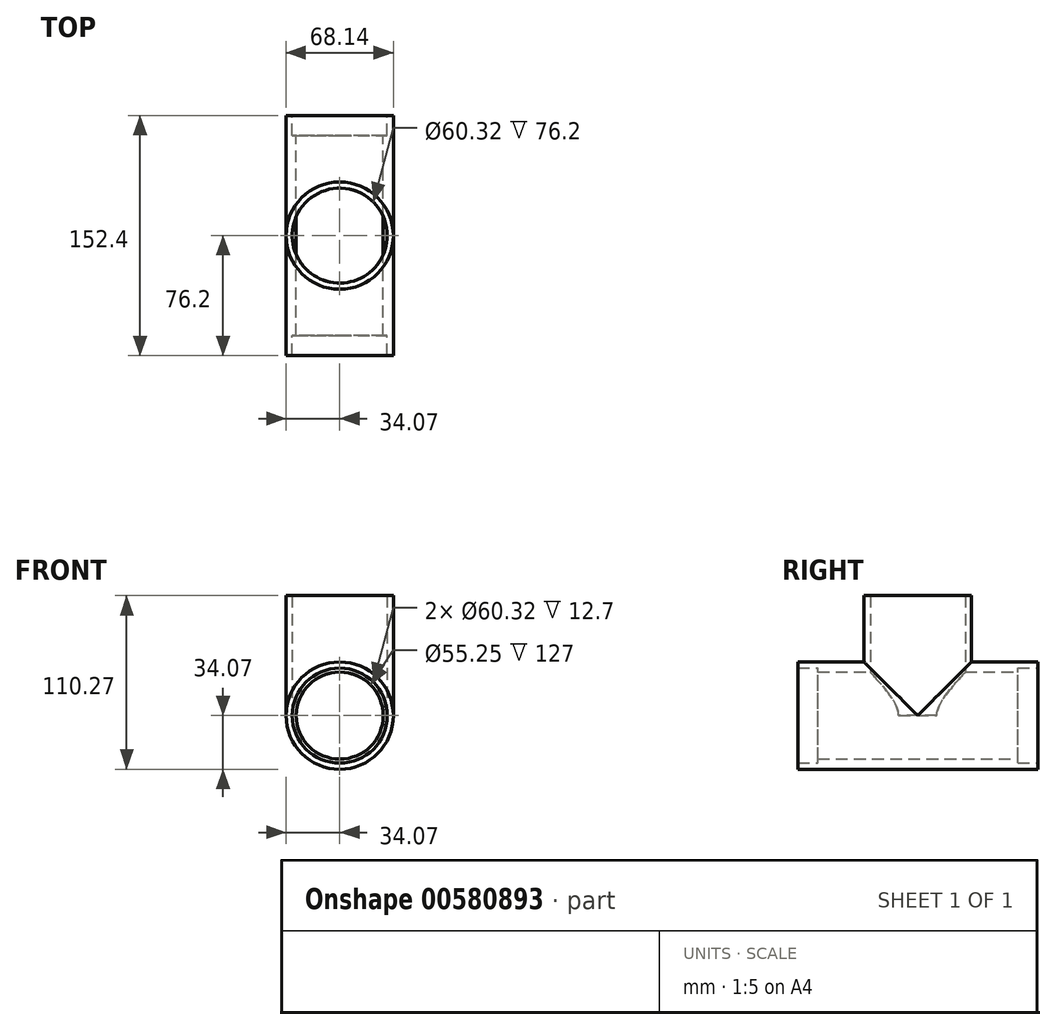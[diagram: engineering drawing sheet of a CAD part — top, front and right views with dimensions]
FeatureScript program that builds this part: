
annotation { "Feature Type Name" : "Feature", "Feature Type Description" : "" }
export const myFeature = defineFeature(function(context is Context, id is Id, definition is map)
    precondition{}
    {
        {
            var Q0;
            Q0=qCreatedBy(makeId("Front.planeOp"),FACE);
            var sketch = newSketch(context, id + "F0", { "sketchPlane" : qUnion([Q0])});
            skCircle(sketch, "E0", {"center": v(0, 0) * mm, "radius": 30.16 * mm});
            skCircle(sketch, "E1.0", {"center": v(0, 0) * mm, "radius": 34.07 * mm});
            skSolve(sketch);
        }
        {
            var Q0;
            Q0 = qSketchRegion(id + "F0", true);
            extrude(context, id + "F1", {"entities" : qUnion([Q0]), "endBound" : BoundingType.SYMMETRIC, "depth" : 152.4 * mm, "offsetDistance" : 25 * mm});
        }
        {
            var Q0;
            Q0=qCreatedBy(makeId("Top.planeOp"),FACE);
            var sketch = newSketch(context, id + "F2", { "sketchPlane" : qUnion([Q0])});
            skCircle(sketch, "E2", {"center": v(0, 0) * mm, "radius": 30.16 * mm});
            skCircle(sketch, "E3.0", {"center": v(0, 0) * mm, "radius": 34.07 * mm});
            skSolve(sketch);
        }
        {
            var Q0;
            Q0 = qSketchRegion(id + "F2", true);
            extrude(context, id + "F3", {"entities" : qUnion([Q0]), "operationType" : NewBodyOperationType.ADD, "depth" : 76.2 * mm, "offsetDistance" : 25 * mm});
        }
        {
            var Q0;
            Q0=qCreatedBy(makeId("Front.planeOp"),FACE);
            var sketch = newSketch(context, id + "F4", { "sketchPlane" : qUnion([Q0])});
            skCircle(sketch, "E4.0", {"center": v(0, 0) * mm, "radius": 27.62 * mm});
            skCircle(sketch, "E5.0", {"center": v(0, 0) * mm, "radius": 34.07 * mm});
            skSolve(sketch);
        }
        {
            var Q0;
            Q0 = qSketchRegion(id + "F4", true);
            extrude(context, id + "F5", {"entities" : qUnion([Q0]), "operationType" : NewBodyOperationType.ADD, "endBound" : BoundingType.SYMMETRIC, "depth" : 127 * mm, "offsetDistance" : 25 * mm});
        }
        {
            var Q0;
            Q0=makeQuery(id+"F3.opExtrude","CAP_FACE",FACE,{"disambiguationData":[OSD([sQuery(id+"F2.wireOp",EDGE,"E2"),sQuery(id+"F2.wireOp",EDGE,"E3.0")])],"isStart":false});
            var sketch = newSketch(context, id + "F6", { "sketchPlane" : qUnion([Q0])});
            skCircle(sketch, "E6.0", {"center": v(0, 0) * mm, "radius": 30.16 * mm});
            skSolve(sketch);
        }
        {
            var Q0;
            Q0 = qSketchRegion(id + "F6", true);
            var Q1;
            Q1=makeQuery(id+"F3.boolean.opBoolean","SPLIT",FACE,{"disambiguationData":[OD(1.0)],"derivedFrom":makeQuery(id+"F3.opExtrude","CAP_FACE",FACE,{"disambiguationData":[OSD([sQuery(id+"F2.wireOp",EDGE,"E2"),sQuery(id+"F2.wireOp",EDGE,"E3.0")])],"isStart":true})});
            extrude(context, id + "F7", {"entities" : qUnion([Q0]), "operationType" : NewBodyOperationType.REMOVE, "endBound" : BoundingType.UP_TO_SURFACE, "oppositeDirection" : true, "depth" : 83.9 * mm, "endBoundEntityFace" : qUnion([Q1]), "offsetDistance" : 25 * mm});
        }
        {
            var Q0;
            Q0=qCreatedBy(makeId("Front.planeOp"),FACE);
            var sketch = newSketch(context, id + "F8", { "sketchPlane" : qUnion([Q0])});
            skCircle(sketch, "E7.0", {"center": v(0, 0) * mm, "radius": 27.62 * mm});
            skSolve(sketch);
        }
        {
            var Q0;
            Q0 = qSketchRegion(id + "F8", true);
            extrude(context, id + "F9", {"entities" : qUnion([Q0]), "operationType" : NewBodyOperationType.REMOVE, "endBound" : BoundingType.SYMMETRIC, "depth" : 287.2 * mm, "offsetDistance" : 25 * mm});
        }
    });
